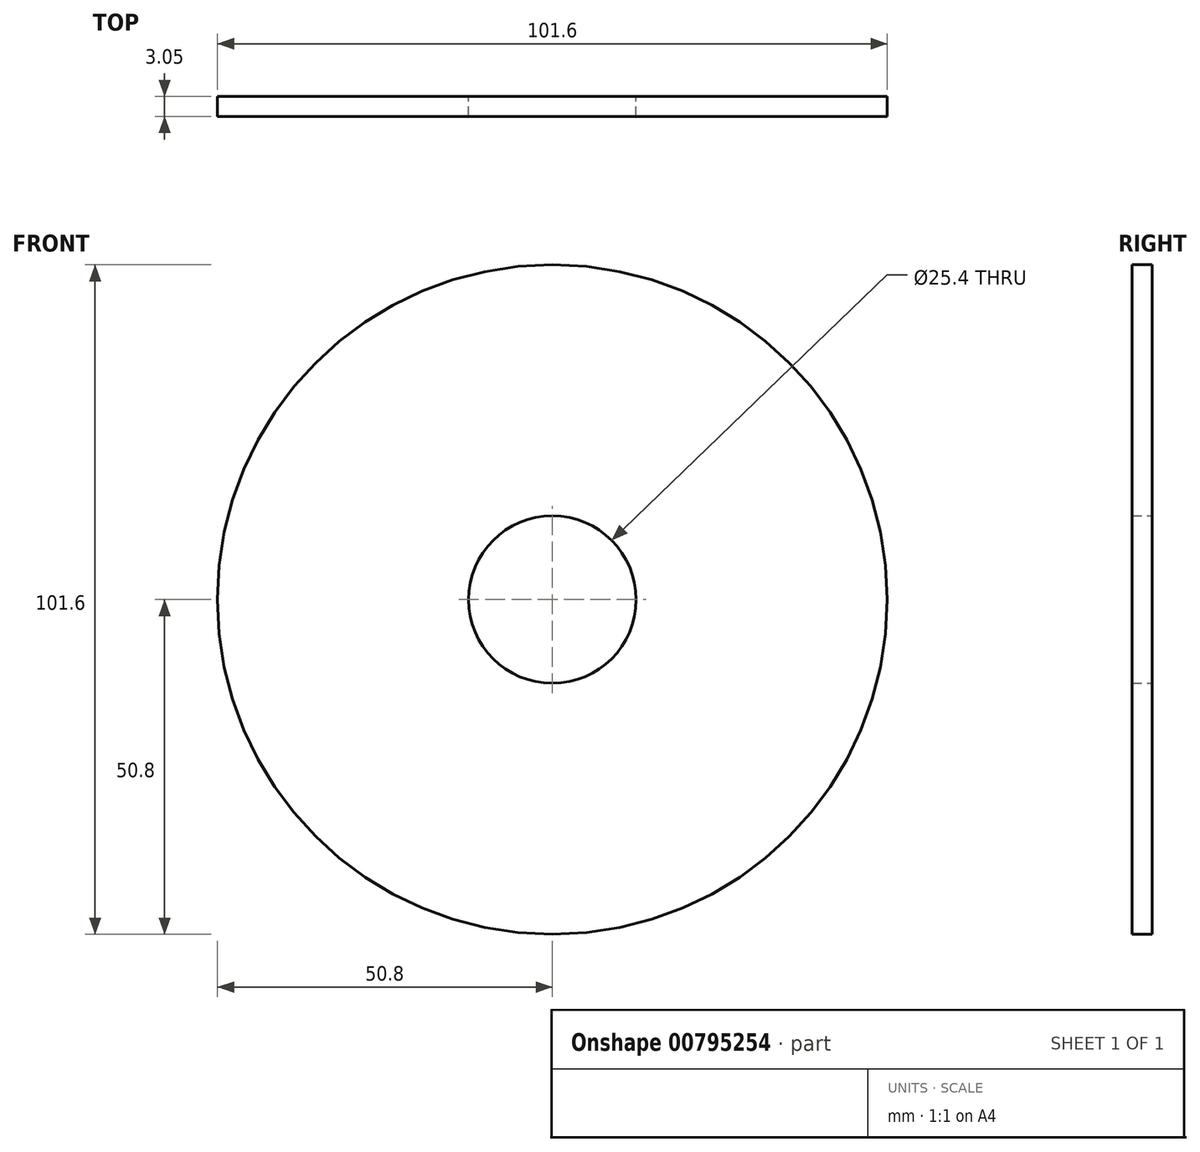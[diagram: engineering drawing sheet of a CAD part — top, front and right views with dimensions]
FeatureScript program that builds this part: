
annotation { "Feature Type Name" : "Feature", "Feature Type Description" : "" }
export const myFeature = defineFeature(function(context is Context, id is Id, definition is map)
    precondition{}
    {
        {
            var Q0;
            Q0=qCreatedBy(makeId("Front.planeOp"),FACE);
            var sketch = newSketch(context, id + "F0", { "sketchPlane" : qUnion([Q0])});
            skCircle(sketch, "E0", {"center": v(0, 0) * mm, "radius": 50.8 * mm});
            skCircle(sketch, "E1", {"center": v(0, 0) * mm, "radius": 12.7 * mm});
            skSolve(sketch);
        }
        {
            var Q0;
            Q0=makeQuery(id+"F0.imprint","IMPRINT",FACE,{"disambiguationData":[TD([[makeQuery(id+"F0.imprint","IMPRINT",EDGE,{"derivedFrom":sQuery(id+"F0.wireOp",EDGE,"E0")}),1.0]])]});
            extrude(context, id + "F1", {"entities" : qUnion([Q0]), "depth" : 3.05 * mm, "offsetDistance" : 25.4 * mm});
        }
    });
